# Revit family: Haworth_ComposeEcho_MarkerboardTablet
name_source: partatom
category: Furniture Systems
units: mm (PartAtom-declared; Revit-internal decimal feet)

## family parameters
Always vertical = Yes
Cut with Voids When Loaded = No
OmniClass Number = 23.40.70.14.64.21
OmniClass Title = Systems Furniture
Part Type = Normal
Room Calculation Point = No
Round Connector Dimension = Use Diameter
Shared = No
Work Plane-Based = No

## types (2) — shared parameters
Actual Depth = 0.47 "
Assembly Code = E2020500
Description = Haworth - Compose Echo - Markerboard Tablet
Manufacturer = Haworth
Model = Haworth - Compose Echo
Revision Number = 1
Size = Verify Final Dim. w/ Haworth
Sustainability Info = https://library.haworth.com
URL = www.haworth.com
URL - Product = http://www.haworth.com
Warranty = http://www.haworth.com

## per-type parameters (varying)
| type | Actual Height | Actual Width | Large Screen | Small Screen |
| 22h 30w | 22 " | 30 " | No | Yes |
| 30h 48w | 30 " | 48 " | Yes | No |

## geometry (parser evidence)
native form markers: Sweep x6
no freeform markers — native parametric forms only
